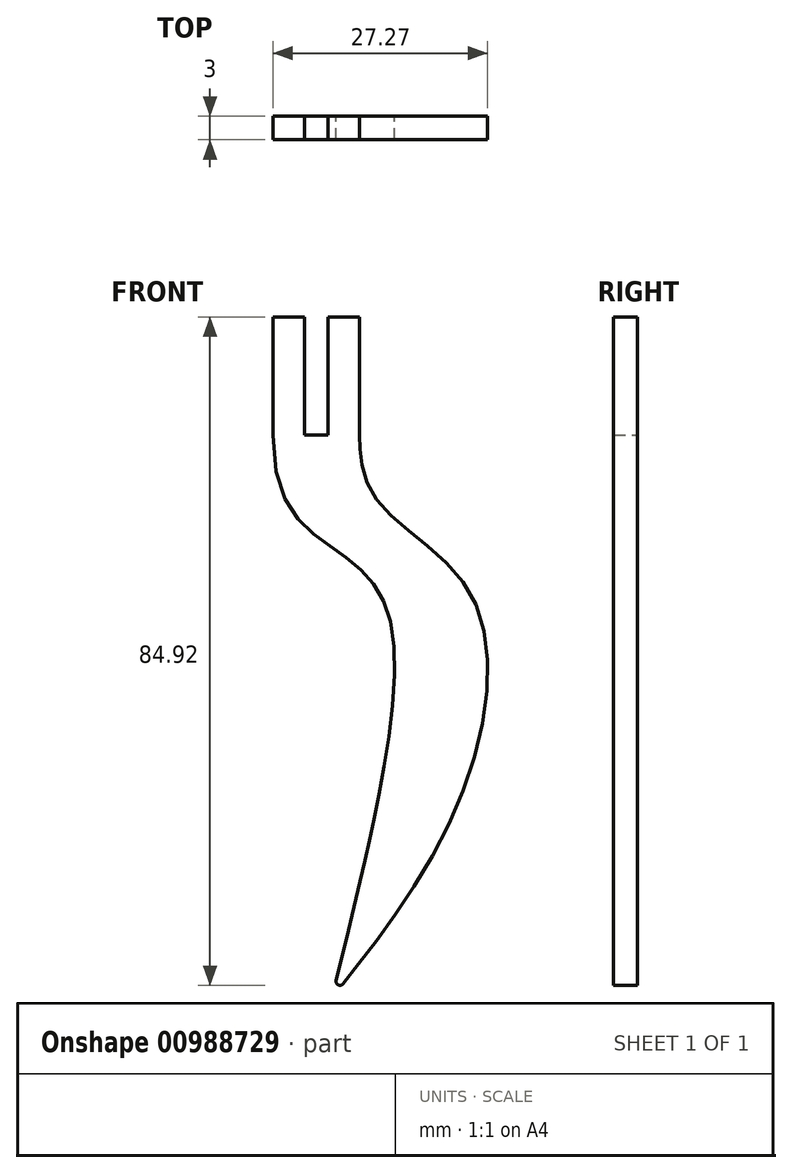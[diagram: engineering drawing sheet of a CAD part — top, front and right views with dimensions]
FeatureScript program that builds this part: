
annotation { "Feature Type Name" : "Feature", "Feature Type Description" : "" }
export const myFeature = defineFeature(function(context is Context, id is Id, definition is map)
    precondition{}
    {
        {
            var Q0;
            Q0=qCreatedBy(makeId("Front.planeOp"),FACE);
            var sketch = newSketch(context, id + "F0", { "sketchPlane" : qUnion([Q0])});
            skLineSegment(sketch, "E0.bottom", {"start": v(0, 0) * mm, "end": v(-4, 0) * mm});
            skLineSegment(sketch, "E0.top", {"start": v(0, 15) * mm, "end": v(-4, 15) * mm});
            skLineSegment(sketch, "E0.left", {"start": v(0, 0) * mm, "end": v(0, 15) * mm});
            skLineSegment(sketch, "E0.right", {"start": v(-4, 0) * mm, "end": v(-4, 15) * mm});
            skLineSegment(sketch, "E1.bottom", {"start": v(-7, 0) * mm, "end": v(-11, 0) * mm});
            skLineSegment(sketch, "E1.top", {"start": v(-7, 15) * mm, "end": v(-11, 15) * mm});
            skLineSegment(sketch, "E1.left", {"start": v(-7, 0) * mm, "end": v(-7, 15) * mm});
            skLineSegment(sketch, "E1.right", {"start": v(-11, 0) * mm, "end": v(-11, 15) * mm});
            skFitSpline(sketch, "E2", {"points": [v(-11, 0) * mm, v(-2.5, -15) * mm, v(4, -24) * mm, v(2, -48) * mm, v(-3.5, -71.5) * mm], "startDerivative": vector(0, -125) * mm, "endDerivative": vector(-36.98, -152.34) * mm});
            skFitSpline(sketch, "E3", {"points": [v(0, 0) * mm, v(2, -8) * mm, v(14, -20) * mm, v(12, -48) * mm, v(-3.5, -71.5) * mm], "startDerivative": vector(0, -36.76) * mm, "endDerivative": vector(-34.82, -43.94) * mm});
            skLineSegment(sketch, "E4", {"start": v(-7, 0) * mm, "end": v(-4, 0) * mm});
            skLineSegment(sketch, "E5", {"start": v(-5.5, 0) * mm, "end": v(-5.5, -71.5) * mm, "construction": true});
            skSolve(sketch);
        }
        {
            var Q0;
            Q0=makeQuery(id+"F0.imprint","IMPRINT",FACE,{"disambiguationData":[TD([[makeQuery(id+"F0.imprint","IMPRINT",EDGE,{"derivedFrom":sQuery(id+"F0.wireOp",EDGE,"E1.bottom")}),-1.0]])]});
            var Q1;
            Q1=makeQuery(id+"F0.imprint","IMPRINT",FACE,{"disambiguationData":[TD([[makeQuery(id+"F0.imprint","IMPRINT",EDGE,{"derivedFrom":sQuery(id+"F0.wireOp",EDGE,"E0.bottom")}),1.0]])]});
            var Q2;
            Q2=makeQuery(id+"F0.imprint","IMPRINT",FACE,{"disambiguationData":[TD([[makeQuery(id+"F0.imprint","IMPRINT",EDGE,{"derivedFrom":sQuery(id+"F0.wireOp",EDGE,"E0.bottom")}),-1.0]])]});
            extrude(context, id + "F1", {"entities" : qUnion([Q0, Q1, Q2]), "depth" : 3 * mm, "offsetDistance" : 25 * mm});
        }
        {
            var Q0;
            Q0=makeQuery(id+"F1.opExtrude","SWEPT_EDGE",EDGE,{"disambiguationData":[OSD([sQuery(id+"F0.wireOp",EDGE,"E2"),sQuery(id+"F0.wireOp",EDGE,"E3")])]});
            fillet(context, id + "F2", {"entities" : qUnion([Q0]), "radius" : .5 * mm, "tangentPropagation" : true, "allowEdgeOverflow" : false});
        }
    });
